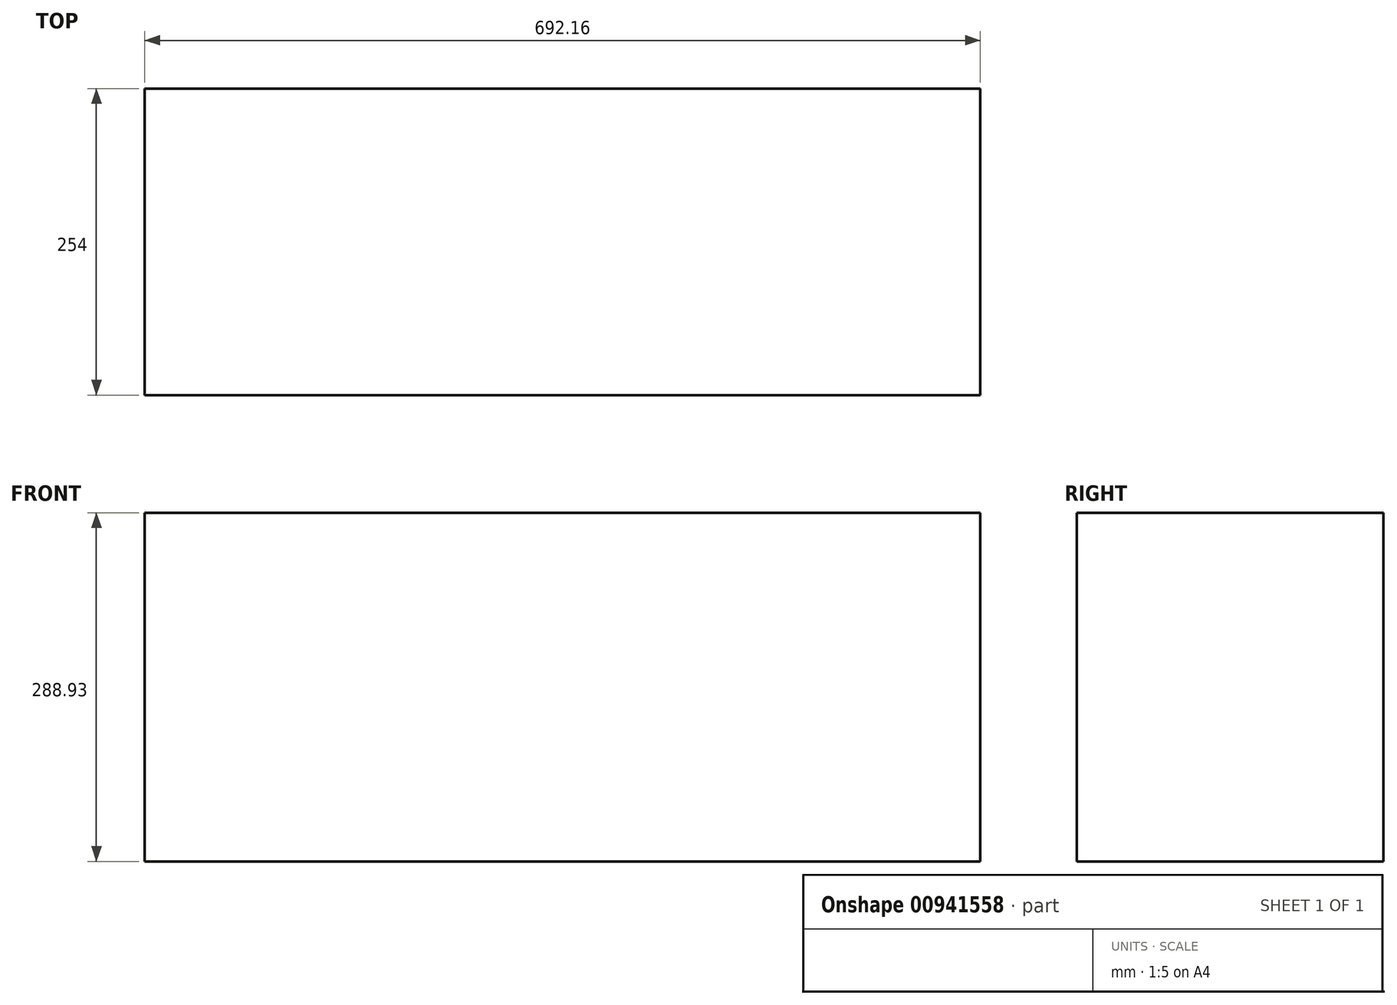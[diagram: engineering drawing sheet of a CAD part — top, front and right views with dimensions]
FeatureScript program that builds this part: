
annotation { "Feature Type Name" : "Feature", "Feature Type Description" : "" }
export const myFeature = defineFeature(function(context is Context, id is Id, definition is map)
    precondition{}
    {
        {
            var Q0;
            Q0=qCreatedBy(makeId("Top.planeOp"),FACE);
            var sketch = newSketch(context, id + "F0", { "sketchPlane" : qUnion([Q0])});
            skLineSegment(sketch, "E0.bottom", {"start": v(346.08, 127) * mm, "end": v(-346.08, 127) * mm});
            skLineSegment(sketch, "E0.top", {"start": v(346.08, -127) * mm, "end": v(-346.08, -127) * mm});
            skLineSegment(sketch, "E0.left", {"start": v(346.08, 127) * mm, "end": v(346.08, -127) * mm});
            skLineSegment(sketch, "E0.right", {"start": v(-346.08, 127) * mm, "end": v(-346.08, -127) * mm});
            skPoint(sketch, "E0.middle", {"position": v(0, 0) * mm});
            skSolve(sketch);
        }
        {
            var Q0;
            Q0 = qSketchRegion(id + "F0", true);
            extrude(context, id + "F1", {"entities" : qUnion([Q0]), "depth" : 288.93 * mm, "offsetDistance" : 25.4 * mm});
        }
    });
